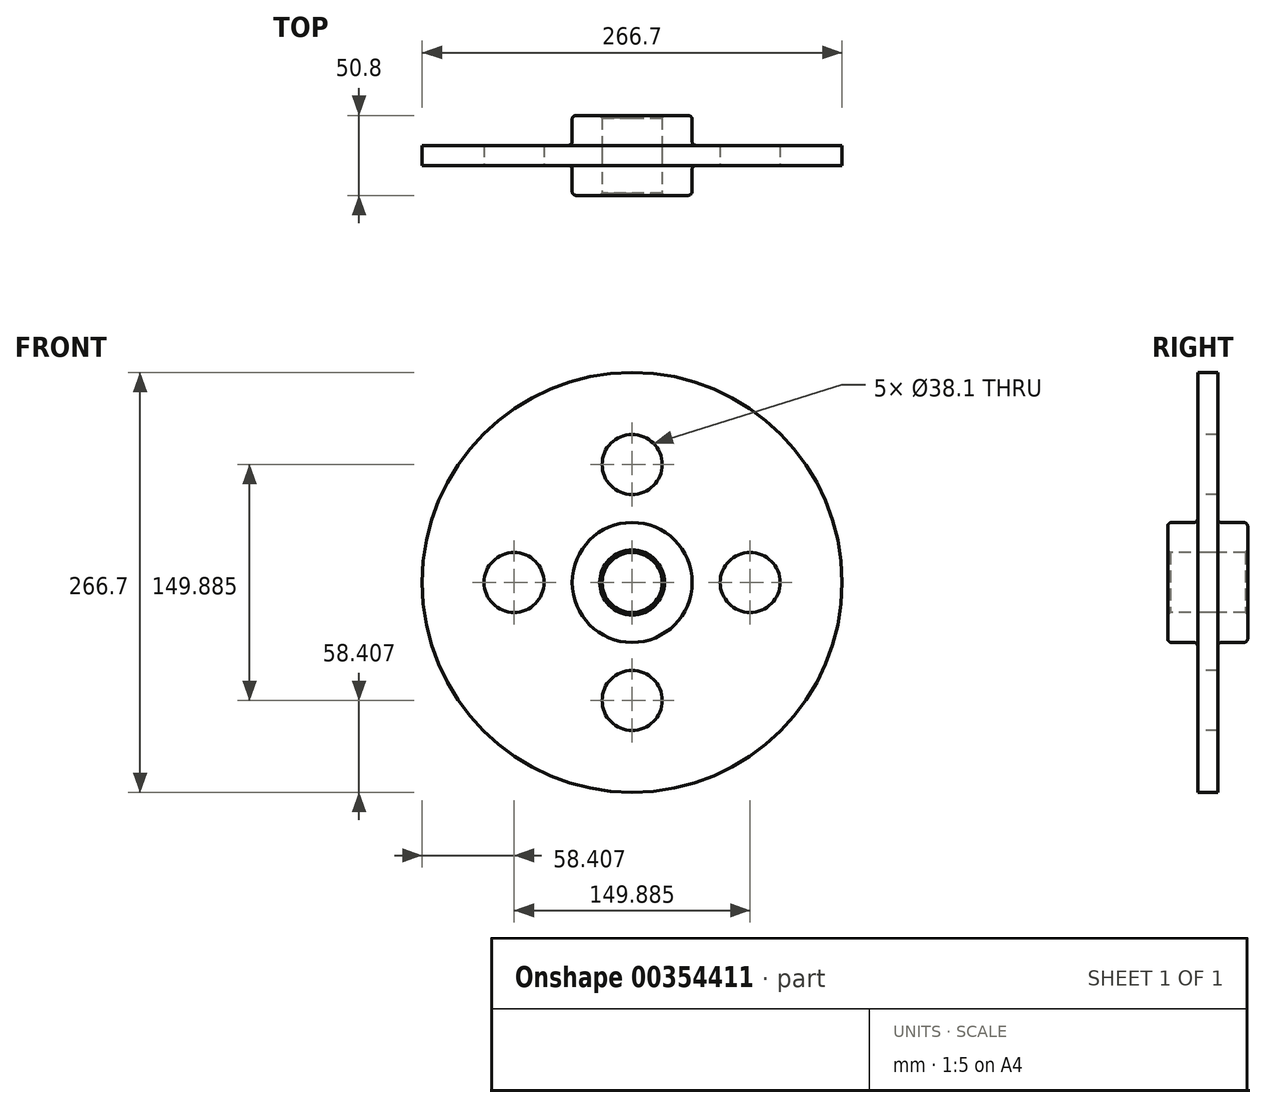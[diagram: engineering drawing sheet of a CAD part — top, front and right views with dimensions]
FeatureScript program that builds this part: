
annotation { "Feature Type Name" : "Feature", "Feature Type Description" : "" }
export const myFeature = defineFeature(function(context is Context, id is Id, definition is map)
    precondition{}
    {
        {
            var Q0;
            Q0=qCreatedBy(makeId("Right.planeOp"),FACE);
            var sketch = newSketch(context, id + "F0", { "sketchPlane" : qUnion([Q0])});
            skLineSegment(sketch, "E0", {"start": v(0, 0) * mm, "end": v(76.78, 0) * mm, "construction": true});
            skLineSegment(sketch, "E1.0", {"start": v(0, 19.05) * mm, "end": v(25.4, 19.05) * mm});
            skLineSegment(sketch, "E2.0", {"start": v(6.35, 38.1) * mm, "end": v(25.4, 38.1) * mm});
            skLineSegment(sketch, "E3.0", {"start": v(6.35, 107.95) * mm, "end": v(12.7, 107.95) * mm});
            skLineSegment(sketch, "E4.0", {"start": v(0, 133.35) * mm, "end": v(12.7, 133.35) * mm});
            skLineSegment(sketch, "E5", {"start": v(0, 133.35) * mm, "end": v(0, 0) * mm, "construction": true});
            skLineSegment(sketch, "E6.0", {"start": v(25.4, 38.1) * mm, "end": v(25.4, 19.05) * mm});
            skLineSegment(sketch, "E7.0", {"start": v(6.35, 133.35) * mm, "end": v(6.35, 38.1) * mm});
            skLineSegment(sketch, "E8.0", {"start": v(12.7, 133.35) * mm, "end": v(12.7, 107.95) * mm});
            skLineSegment(sketch, "E9.MirrorCS", {"start": v(-6.35, 133.35) * mm, "end": v(-6.35, 38.1) * mm});
            skLineSegment(sketch, "E10.MirrorCS", {"start": v(-25.4, 38.1) * mm, "end": v(-25.4, 19.05) * mm});
            skLineSegment(sketch, "E11.MirrorCS", {"start": v(-6.35, 38.1) * mm, "end": v(-25.4, 38.1) * mm});
            skLineSegment(sketch, "E12.MirrorCS", {"start": v(0, 19.05) * mm, "end": v(-25.4, 19.05) * mm});
            skLineSegment(sketch, "E13.MirrorCS", {"start": v(-12.7, 133.35) * mm, "end": v(-12.7, 107.95) * mm});
            skLineSegment(sketch, "E14.MirrorCS", {"start": v(0, 133.35) * mm, "end": v(0, 266.7) * mm, "construction": true});
            skLineSegment(sketch, "E15.MirrorCS", {"start": v(-12.7, 133.35) * mm, "end": v(-12.7, 158.75) * mm});
            skLineSegment(sketch, "E16.MirrorCS", {"start": v(-6.35, 133.35) * mm, "end": v(-6.35, 228.6) * mm});
            skLineSegment(sketch, "E17.MirrorCS", {"start": v(-6.35, 228.6) * mm, "end": v(-25.4, 228.6) * mm});
            skLineSegment(sketch, "E18", {"start": v(12.7, 133.35) * mm, "end": v(-12.7, 133.35) * mm});
            skSolve(sketch);
        }
        {
            var Q0;
            {var subQ1=sQuery(id+"F0.wireOp",EDGE,"E2.0");Q0=makeQuery(id+"F0.imprint","IMPRINT",FACE,{"disambiguationData":[TD([[makeQuery(id+"F0.imprint","IMPRINT",EDGE,{"derivedFrom":subQ1}),-1.0]])]});}
            var Q1;
            Q1=sQuery(id+"F0.wireOp",EDGE,"E0");
            revolve(context, id + "F1", {"entities" : qUnion([Q0]), "axis" : qUnion([Q1]), "revolveType" : RevolveType.FULL});
        }
        {
            var Q0;
            Q0=makeQuery(id+"F1.opRevolve","SWEPT_FACE",FACE,{"disambiguationData":[OSD([sQuery(id+"F0.wireOp",EDGE,"E9.MirrorCS")])]});
            var sketch = newSketch(context, id + "F2", { "sketchPlane" : qUnion([Q0])});
            skLineSegment(sketch, "E19", {"start": v(0, 0) * mm, "end": v(0, 74.94) * mm});
            skCircle(sketch, "E20", {"center": v(0, 74.94) * mm, "radius": 19.05 * mm});
            skCircle(sketch, "E21.1.0", {"center": v(-74.94, 0) * mm, "radius": 19.05 * mm});
            skCircle(sketch, "E21.2.0", {"center": v(0, -74.94) * mm, "radius": 19.05 * mm});
            skCircle(sketch, "E21.3.0", {"center": v(74.94, 0) * mm, "radius": 19.05 * mm});
            skPoint(sketch, "E21.center", {"position": v(0, 0) * mm});
            skSolve(sketch);
        }
        {
            var Q0;
            Q0=makeQuery(id+"F2.imprint","IMPRINT",FACE,{"disambiguationData":[TD([[makeQuery(id+"F2.imprint","IMPRINT",EDGE,{"derivedFrom":sQuery(id+"F2.wireOp",EDGE,"E20")}),1.0]])]});
            var Q1;
            Q1=makeQuery(id+"F2.imprint","IMPRINT",FACE,{"disambiguationData":[TD([[makeQuery(id+"F2.imprint","IMPRINT",EDGE,{"derivedFrom":sQuery(id+"F2.wireOp",EDGE,"E21.1.0")}),1.0]])]});
            var Q2;
            Q2=makeQuery(id+"F2.imprint","IMPRINT",FACE,{"disambiguationData":[TD([[makeQuery(id+"F2.imprint","IMPRINT",EDGE,{"derivedFrom":sQuery(id+"F2.wireOp",EDGE,"E21.2.0")}),1.0]])]});
            var Q3;
            Q3=makeQuery(id+"F2.imprint","IMPRINT",FACE,{"disambiguationData":[TD([[makeQuery(id+"F2.imprint","IMPRINT",EDGE,{"derivedFrom":sQuery(id+"F2.wireOp",EDGE,"E21.3.0")}),1.0]])]});
            extrude(context, id + "F3", {"entities" : qUnion([Q0, Q1, Q2, Q3]), "operationType" : NewBodyOperationType.REMOVE, "oppositeDirection" : true, "depth" : 25.4 * mm});
        }
        {
            var Q0;
            Q0=makeQuery(id+"F1.opRevolve","SWEPT_EDGE",EDGE,{"disambiguationData":[OSD([sQuery(id+"F0.wireOp",EDGE,"E9.MirrorCS"),sQuery(id+"F0.wireOp",EDGE,"E11.MirrorCS")])]});
            var Q1;
            Q1=makeQuery(id+"F1.opRevolve","SWEPT_EDGE",EDGE,{"disambiguationData":[OSD([sQuery(id+"F0.wireOp",EDGE,"E10.MirrorCS"),sQuery(id+"F0.wireOp",EDGE,"E11.MirrorCS")])]});
            var Q2;
            Q2=makeQuery(id+"F1.opRevolve","SWEPT_EDGE",EDGE,{"disambiguationData":[OSD([sQuery(id+"F0.wireOp",EDGE,"E2.0"),sQuery(id+"F0.wireOp",EDGE,"E7.0")])]});
            var Q3;
            Q3=makeQuery(id+"F1.opRevolve","SWEPT_EDGE",EDGE,{"disambiguationData":[OSD([sQuery(id+"F0.wireOp",EDGE,"E2.0"),sQuery(id+"F0.wireOp",EDGE,"E6.0")])]});
            fillet(context, id + "F4", {"entities" : qUnion([Q0, Q1, Q2, Q3]), "radius" : 2.54 * mm, "tangentPropagation" : true, "allowEdgeOverflow" : false});
        }
        {
            var Q0;
            Q0=makeQuery(id+"F1.opRevolve","SWEPT_EDGE",EDGE,{"disambiguationData":[OSD([sQuery(id+"F0.wireOp",EDGE,"E10.MirrorCS"),sQuery(id+"F0.wireOp",EDGE,"E12.MirrorCS")])]});
            var Q1;
            Q1=makeQuery(id+"F1.opRevolve","SWEPT_EDGE",EDGE,{"disambiguationData":[OSD([sQuery(id+"F0.wireOp",EDGE,"E6.0"),sQuery(id+"F0.wireOp",EDGE,"E1.0")])]});
            chamfer(context, id + "F5", {"entities" : qUnion([Q0, Q1]), "width" : 1.59 * mm, "tangentPropagation" : true});
        }
    });
